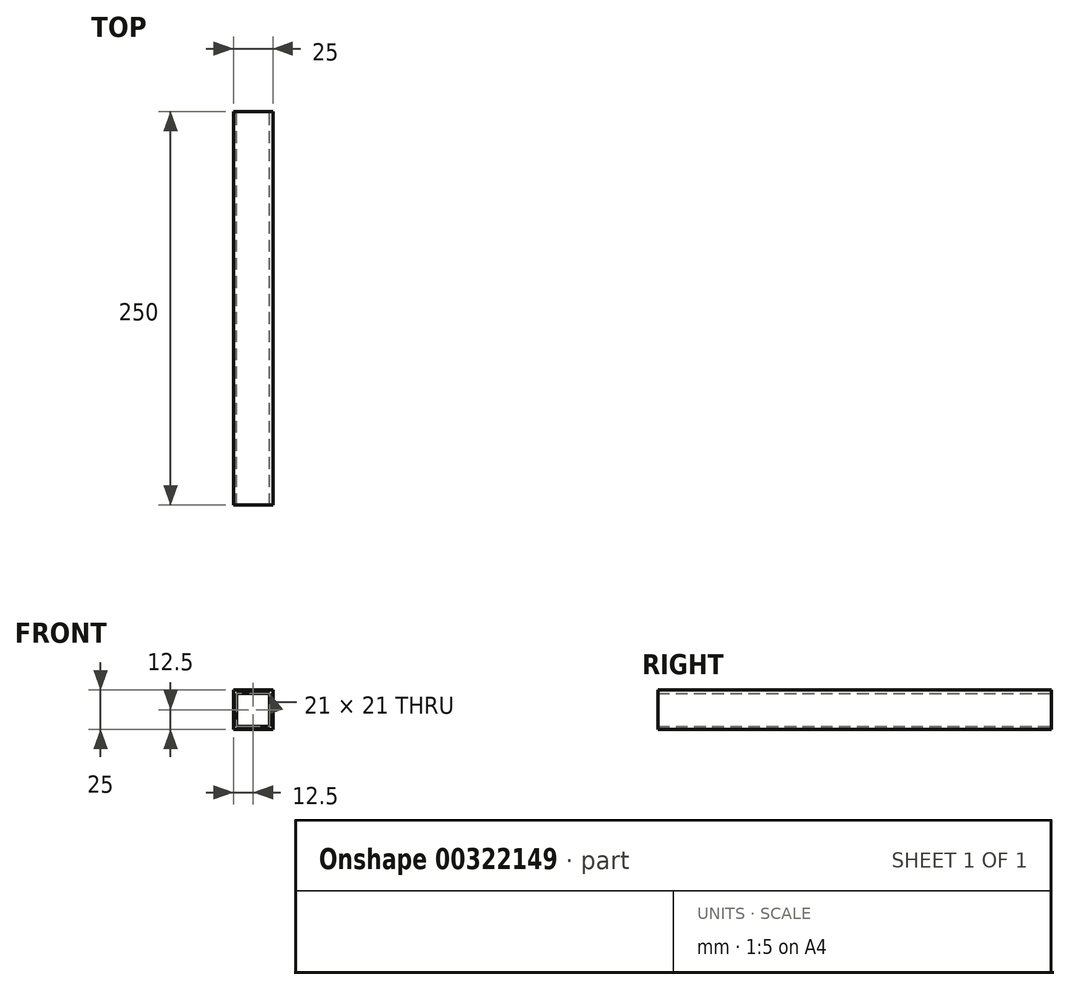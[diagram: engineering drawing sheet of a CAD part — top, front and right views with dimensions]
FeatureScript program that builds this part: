
annotation { "Feature Type Name" : "Feature", "Feature Type Description" : "" }
export const myFeature = defineFeature(function(context is Context, id is Id, definition is map)
    precondition{}
    {
        {
            var Q0;
            Q0=qCreatedBy(makeId("Front.planeOp"),FACE);
            var sketch = newSketch(context, id + "F0", { "sketchPlane" : qUnion([Q0])});
            skLineSegment(sketch, "E0.bottom", {"start": v(-25, 0) * mm, "end": v(0, 0) * mm});
            skLineSegment(sketch, "E0.top", {"start": v(-25, -25) * mm, "end": v(0, -25) * mm});
            skLineSegment(sketch, "E0.left", {"start": v(-25, 0) * mm, "end": v(-25, -25) * mm});
            skLineSegment(sketch, "E0.right", {"start": v(0, 0) * mm, "end": v(0, -25) * mm});
            skLineSegment(sketch, "E1.0", {"start": v(-23, -2) * mm, "end": v(-2, -2) * mm});
            skLineSegment(sketch, "E1.1", {"start": v(-23, -2) * mm, "end": v(-23, -23) * mm});
            skLineSegment(sketch, "E1.2", {"start": v(-23, -23) * mm, "end": v(-2, -23) * mm});
            skLineSegment(sketch, "E1.3", {"start": v(-2, -2) * mm, "end": v(-2, -23) * mm});
            skSolve(sketch);
        }
        {
            var Q0;
            Q0 = qSketchRegion(id + "F0", true);
            extrude(context, id + "F1", {"entities" : qUnion([Q0]), "depth" : 250 * mm});
        }
    });
